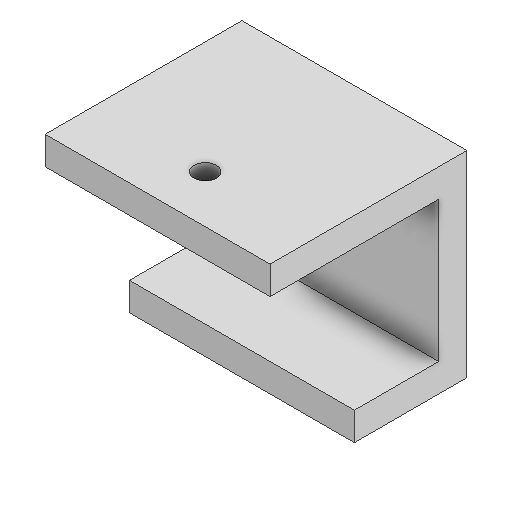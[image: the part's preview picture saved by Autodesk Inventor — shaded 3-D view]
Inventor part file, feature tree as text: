
AUTODESK INVENTOR PART (.ipt)
format: ipt  version: 2025.1 (Build 291241000, 241)  size: 123,392 bytes
history: native  units: mm
features: sketch x5, extrude x4, other x1, hole x1
ambient origin geometry x8: Origin, YZ Plane, XZ Plane, XY Plane, X Axis, Y Axis, Z Axis, Center Point
bodies: Body1 (feature_tree)
feature tree (11):
  other  "Bryła1"
  extrude  "Wyciągnięcie proste1"  Depth=40.0mm
  extrude  "Wyciągnięcie proste2"  Depth=30.0mm
  extrude  "Wyciągnięcie proste3"  Depth=5.0mm TaperAngle=0.0deg
  hole  "Otwór1"  [1 undecoded]
  extrude  "Wyciągnięcie proste4"  Depth=30.0mm TaperAngle=0.0deg
  sketch  "Szkic1"
  sketch  "Szkic2"
  sketch  "Szkic5"
  sketch  "Szkic6"
  sketch  "Szkic7"
note: 1 required parameter value undecoded (feature->parameter linkage not recoverable at this tier; creation-order binding heuristic only, values carry confidence <= 0.55)
